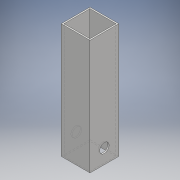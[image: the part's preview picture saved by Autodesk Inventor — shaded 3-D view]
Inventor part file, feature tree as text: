
AUTODESK INVENTOR PART (.ipt)
format: ipt  version: 2018 (Build 220112000, 112)  size: 105,984 bytes
history: native  units: mm
features: sketch x2, other x1, extrude x1, hole x1
ambient origin geometry x8: Origin, YZ Plane, XZ Plane, XY Plane, X Axis, Y Axis, Z Axis, Center Point
bodies: Body1 (feature_tree)
feature tree (5):
  other  "ソリッド1"
  extrude  "押し出し1"  Depth=32.0mm
  hole  "穴1"  [1 undecoded]
  sketch  "スケッチ1"
  sketch  "スケッチ2"
note: 1 required parameter value undecoded (feature->parameter linkage not recoverable at this tier; creation-order binding heuristic only, values carry confidence <= 0.55)
